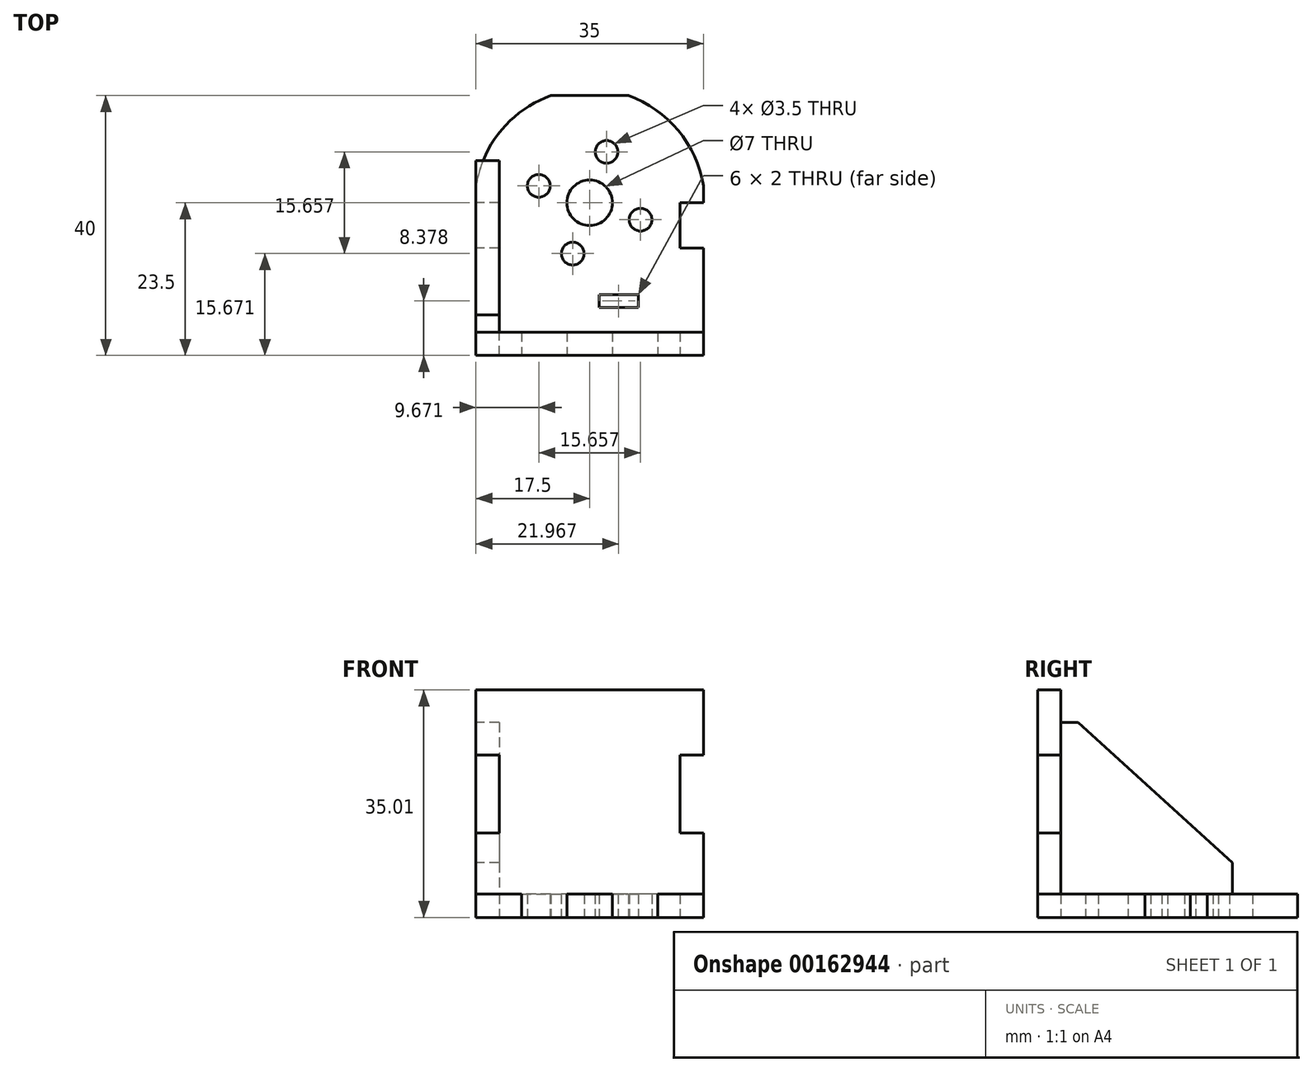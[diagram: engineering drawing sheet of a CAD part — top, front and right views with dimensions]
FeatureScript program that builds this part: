
annotation { "Feature Type Name" : "Feature", "Feature Type Description" : "" }
export const myFeature = defineFeature(function(context is Context, id is Id, definition is map)
    precondition{}
    {
        {
            var Q0;
            Q0=qCreatedBy(makeId("Top.planeOp"),FACE);
            var sketch = newSketch(context, id + "F0", { "sketchPlane" : qUnion([Q0])});
            skLineSegment(sketch, "E0.bottom", {"start": v(0, 0) * mm, "end": v(7, 0) * mm});
            skLineSegment(sketch, "E0.top", {"start": v(11.55, 40) * mm, "end": v(23.45, 40) * mm});
            skLineSegment(sketch, "E0.left", {"start": v(0, 0) * mm, "end": v(0, 16.5) * mm});
            skLineSegment(sketch, "E0.right", {"start": v(35, 0) * mm, "end": v(35, 26.1) * mm});
            skLineSegment(sketch, "E1", {"start": v(17.5, 56.88) * mm, "end": v(17.5, -26.86) * mm, "construction": true});
            skLineSegment(sketch, "E2", {"start": v(7.04, 23.5) * mm, "end": v(27.12, 23.5) * mm, "construction": true});
            skCircle(sketch, "E3", {"center": v(17.5, 23.5) * mm, "radius": 3.5 * mm});
            skCircle(sketch, "E4", {"center": v(17.5, 23.5) * mm, "radius": 8.25 * mm, "construction": true});
            skCircle(sketch, "E5", {"center": v(9.67, 26.1) * mm, "radius": 1.75 * mm});
            skCircle(sketch, "E6.1.0", {"center": v(20.1, 31.33) * mm, "radius": 1.75 * mm});
            skCircle(sketch, "E6.2.0", {"center": v(25.33, 20.9) * mm, "radius": 1.75 * mm});
            skCircle(sketch, "E6.3.0", {"center": v(14.9, 15.67) * mm, "radius": 1.75 * mm});
            skLineSegment(sketch, "E6.anchor1", {"start": v(17.5, 23.5) * mm, "end": v(9.67, 26.1) * mm, "construction": true});
            skLineSegment(sketch, "E6.anchor2", {"start": v(17.5, 23.5) * mm, "end": v(14.9, 15.67) * mm, "construction": true});
            skArc(sketch, "E7", {"start": v(35, 26.1) * mm, "mid": v(31.13, 34.64) * mm, "end": v(23.45, 40) * mm});
            skPoint(sketch, "E8.orphan", {"position": v(0, 40) * mm});
            skArc(sketch, "E9.trimOffspring", {"start": v(11.55, 40) * mm, "mid": v(3.87, 34.64) * mm, "end": v(0, 26.1) * mm});
            skLineSegment(sketch, "E10.top", {"start": v(7, 3.6) * mm, "end": v(14, 3.6) * mm});
            skLineSegment(sketch, "E10.left", {"start": v(7, 0) * mm, "end": v(7, 3.6) * mm});
            skLineSegment(sketch, "E10.right", {"start": v(14, 0) * mm, "end": v(14, 3.6) * mm});
            skLineSegment(sketch, "E11.trimOffspring", {"start": v(14, 0) * mm, "end": v(21, 0) * mm});
            skLineSegment(sketch, "E12.MirrorCS", {"start": v(28, 0) * mm, "end": v(28, 3.6) * mm});
            skLineSegment(sketch, "E13.MirrorCS", {"start": v(28, 3.6) * mm, "end": v(21, 3.6) * mm});
            skLineSegment(sketch, "E14.MirrorCS", {"start": v(21, 0) * mm, "end": v(21, 3.6) * mm});
            skLineSegment(sketch, "E15.trimOffspring", {"start": v(28, 0) * mm, "end": v(35, 0) * mm});
            skLineSegment(sketch, "E16.bottom", {"start": v(0, 23.5) * mm, "end": v(3.6, 23.5) * mm});
            skLineSegment(sketch, "E16.top", {"start": v(0, 16.5) * mm, "end": v(3.6, 16.5) * mm});
            skLineSegment(sketch, "E16.right", {"start": v(3.6, 23.5) * mm, "end": v(3.6, 16.5) * mm});
            skLineSegment(sketch, "E17.MirrorCS", {"start": v(31.4, 23.5) * mm, "end": v(31.4, 16.5) * mm});
            skLineSegment(sketch, "E18.MirrorCS", {"start": v(35, 16.5) * mm, "end": v(31.4, 16.5) * mm});
            skLineSegment(sketch, "E19.MirrorCS", {"start": v(35, 23.5) * mm, "end": v(31.4, 23.5) * mm});
            skLineSegment(sketch, "E20.trimOffspring", {"start": v(0, 23.5) * mm, "end": v(0, 26.1) * mm});
            skLineSegment(sketch, "E21.bottom", {"start": v(18.97, 9.38) * mm, "end": v(24.97, 9.38) * mm});
            skLineSegment(sketch, "E21.top", {"start": v(18.97, 7.38) * mm, "end": v(24.97, 7.38) * mm});
            skLineSegment(sketch, "E21.left", {"start": v(18.97, 9.38) * mm, "end": v(18.97, 7.38) * mm});
            skLineSegment(sketch, "E21.right", {"start": v(24.97, 9.38) * mm, "end": v(24.97, 7.38) * mm});
            skPoint(sketch, "E22", {"position": v(35, 23.5) * mm});
            skSolve(sketch);
        }
        {
            var Q0;
            Q0=qCreatedBy(makeId("Front.planeOp"),FACE);
            var sketch = newSketch(context, id + "F1", { "sketchPlane" : qUnion([Q0])});
            skLineSegment(sketch, "E23.top", {"start": v(0, 35) * mm, "end": v(35, 35) * mm});
            skLineSegment(sketch, "E23.left", {"start": v(0, 3.6) * mm, "end": v(0, 13) * mm});
            skLineSegment(sketch, "E23.right", {"start": v(35, 3.6) * mm, "end": v(35, 35) * mm});
            skLineSegment(sketch, "E24", {"start": v(17.5, -5.4) * mm, "end": v(17.5, 9.42) * mm, "construction": true});
            skLineSegment(sketch, "E25.bottom", {"start": v(0, 25) * mm, "end": v(3.6, 25) * mm});
            skLineSegment(sketch, "E25.top", {"start": v(0, 13) * mm, "end": v(3.6, 13) * mm});
            skLineSegment(sketch, "E25.right", {"start": v(3.6, 25) * mm, "end": v(3.6, 13) * mm});
            skLineSegment(sketch, "E26.trimOffspring", {"start": v(0, 25) * mm, "end": v(0, 35) * mm});
            skLineSegment(sketch, "E27.MirrorCS", {"start": v(31.4, 25) * mm, "end": v(31.4, 13) * mm});
            skLineSegment(sketch, "E28.MirrorCS", {"start": v(35, 25) * mm, "end": v(31.4, 25) * mm});
            skLineSegment(sketch, "E29.MirrorCS", {"start": v(35, 13) * mm, "end": v(31.4, 13) * mm});
            skLineSegment(sketch, "E30.MirrorCS", {"start": v(35, 25) * mm, "end": v(35, 13) * mm});
            skPoint(sketch, "E31", {"position": v(35, 25) * mm});
            skPoint(sketch, "E32", {"position": v(35, 13) * mm});
            skLineSegment(sketch, "E33", {"start": v(7, 0) * mm, "end": v(28, 0) * mm});
            skLineSegment(sketch, "E34", {"start": v(0, 3.6) * mm, "end": v(7, 3.6) * mm});
            skLineSegment(sketch, "E35", {"start": v(35, 3.6) * mm, "end": v(28, 3.6) * mm});
            skLineSegment(sketch, "E36", {"start": v(7, 3.6) * mm, "end": v(7, 0) * mm});
            skLineSegment(sketch, "E37", {"start": v(14, 3.6) * mm, "end": v(14, 0) * mm});
            skLineSegment(sketch, "E38.MirrorCS", {"start": v(21, 3.6) * mm, "end": v(21, 0) * mm});
            skLineSegment(sketch, "E39.MirrorCS", {"start": v(28, 3.6) * mm, "end": v(28, 0) * mm});
            skLineSegment(sketch, "E40.trimOffspring", {"start": v(14, 3.6) * mm, "end": v(21, 3.6) * mm});
            skLineSegment(sketch, "E41.trimOffspring", {"start": v(28, 3.6) * mm, "end": v(35, 3.6) * mm});
            skLineSegment(sketch, "E42.trimOffspring", {"start": v(21, 3.6) * mm, "end": v(14, 3.6) * mm});
            skSolve(sketch);
        }
        {
            var Q0;
            {var subQ0=sQuery(id+"F1.wireOp",EDGE,"E23.top");Q0=makeQuery(id+"F1.imprint","IMPRINT",FACE,{"disambiguationData":[TD([[makeQuery(id+"F1.imprint","IMPRINT",EDGE,{"derivedFrom":subQ0}),-1.0]])]});}
            extrude(context, id + "F2", {"entities" : qUnion([Q0]), "oppositeDirection" : true, "depth" : 3.6 * mm});
        }
        {
            var Q0;
            Q0=makeQuery(id+"F0.imprint","IMPRINT",FACE,{"disambiguationData":[TD([[makeQuery(id+"F0.imprint","IMPRINT",EDGE,{"derivedFrom":sQuery(id+"F0.wireOp",EDGE,"E0.bottom")}),1.0]])]});
            extrude(context, id + "F3", {"entities" : qUnion([Q0]), "depth" : 3.6 * mm});
        }
        {
            var Q0;
            Q0=qCreatedBy(makeId("Right.planeOp"),FACE);
            var sketch = newSketch(context, id + "F4", { "sketchPlane" : qUnion([Q0])});
            skLineSegment(sketch, "E43.bottom", {"start": v(3.6, 30) * mm, "end": v(6.26, 30) * mm});
            skLineSegment(sketch, "E43.top", {"start": v(16.5, 0) * mm, "end": v(23.5, 0) * mm});
            skLineSegment(sketch, "E43.left", {"start": v(0, 25) * mm, "end": v(0, 13) * mm});
            skLineSegment(sketch, "E43.right", {"start": v(30, 8.4) * mm, "end": v(30, 3.6) * mm});
            skLineSegment(sketch, "E44", {"start": v(3.6, 30) * mm, "end": v(3.6, 3.6) * mm});
            skLineSegment(sketch, "E45", {"start": v(3.6, 3.6) * mm, "end": v(16.5, 3.6) * mm});
            skLineSegment(sketch, "E46", {"start": v(16.5, 3.6) * mm, "end": v(16.5, 0) * mm});
            skLineSegment(sketch, "E47", {"start": v(23.5, 0) * mm, "end": v(23.5, 3.6) * mm});
            skLineSegment(sketch, "E48", {"start": v(23.5, 3.6) * mm, "end": v(30, 3.6) * mm});
            skLineSegment(sketch, "E49", {"start": v(0, 25) * mm, "end": v(3.6, 25) * mm});
            skLineSegment(sketch, "E50", {"start": v(0, 13) * mm, "end": v(3.6, 13) * mm});
            skLineSegment(sketch, "E51", {"start": v(6.26, 30) * mm, "end": v(30, 8.4) * mm});
            skPoint(sketch, "E52.orphan", {"position": v(30, 0) * mm});
            skPoint(sketch, "E53.orphan", {"position": v(0, 0) * mm});
            skPoint(sketch, "E54.orphan", {"position": v(0, 30) * mm});
            skSolve(sketch);
        }
        {
            var Q0;
            Q0=makeQuery(id+"F4.imprint","IMPRINT",FACE,{"disambiguationData":[TD([[makeQuery(id+"F4.imprint","IMPRINT",EDGE,{"derivedFrom":sQuery(id+"F4.wireOp",EDGE,"E43.right")}),-1.0]])]});
            var Q1;
            Q1=makeQuery(id+"F4.imprint","IMPRINT",FACE,{"disambiguationData":[TD([[makeQuery(id+"F4.imprint","IMPRINT",EDGE,{"derivedFrom":sQuery(id+"F4.wireOp",EDGE,"E43.left")}),1.0]])]});
            extrude(context, id + "F5", {"entities" : qUnion([Q0, Q1]), "depth" : 3.6 * mm});
        }
    });
